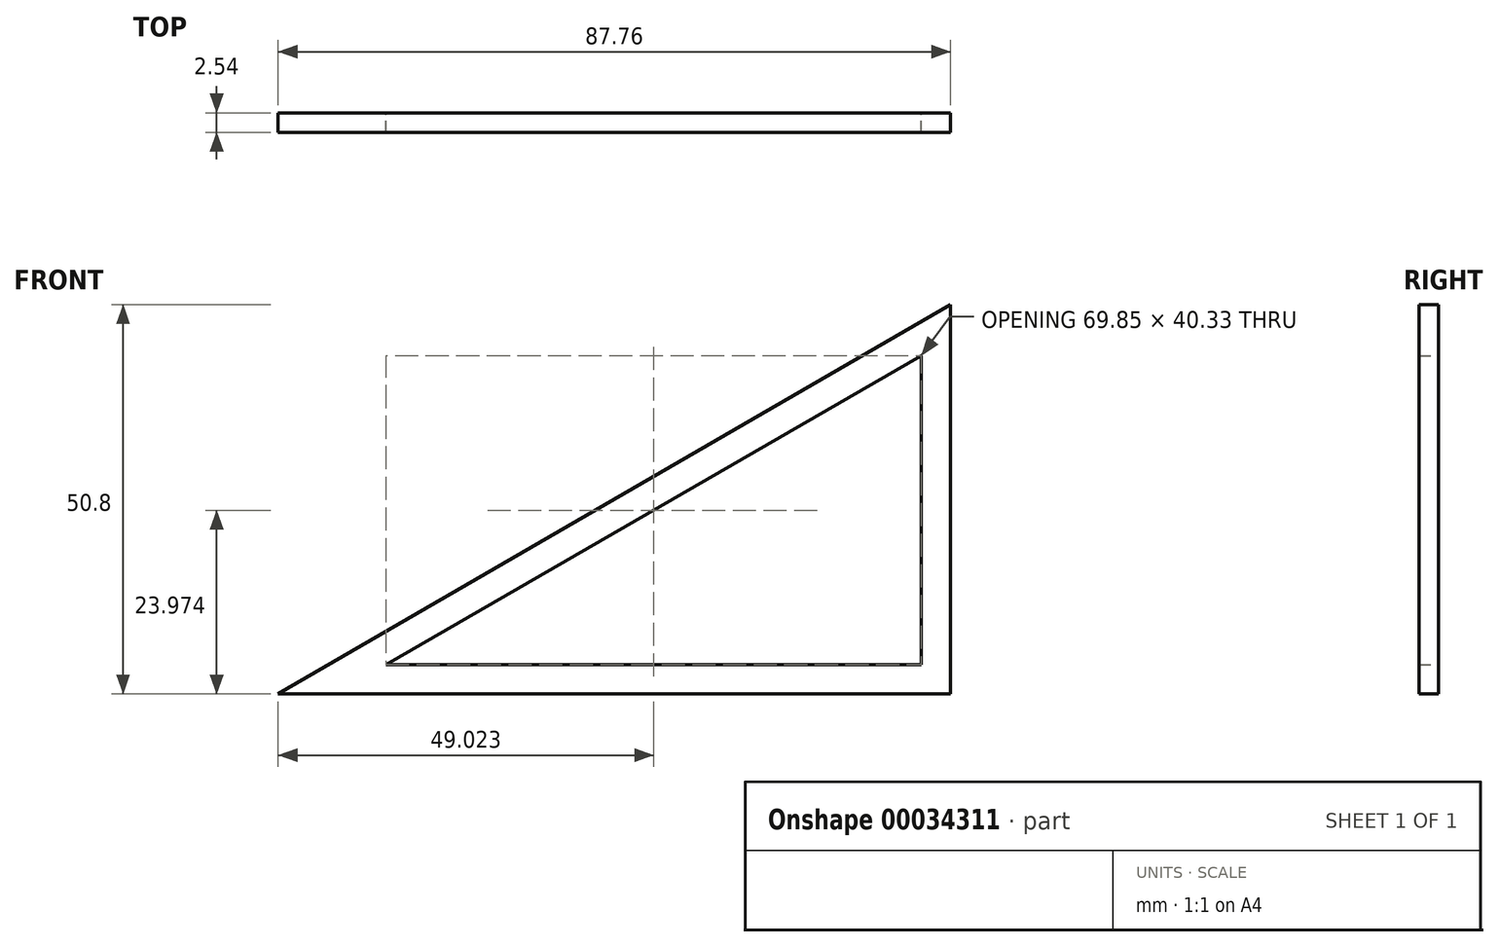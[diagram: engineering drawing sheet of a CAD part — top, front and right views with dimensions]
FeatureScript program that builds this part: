
annotation { "Feature Type Name" : "Feature", "Feature Type Description" : "" }
export const myFeature = defineFeature(function(context is Context, id is Id, definition is map)
    precondition{}
    {
        {
            var Q0;
            Q0=qCreatedBy(makeId("Front.planeOp"),FACE);
            var sketch = newSketch(context, id + "F0", { "sketchPlane" : qUnion([Q0])});
            skLineSegment(sketch, "E0", {"start": v(0, 0) * mm, "end": v(87.76, 0) * mm});
            skLineSegment(sketch, "E1", {"start": v(87.76, 0) * mm, "end": v(87.76, 50.8) * mm});
            skLineSegment(sketch, "E2", {"start": v(87.76, 50.8) * mm, "end": v(0, 0) * mm});
            skLineSegment(sketch, "E3", {"start": v(43.88, 0) * mm, "end": v(43.88, 0) * mm});
            skLineSegment(sketch, "E4", {"start": v(87.76, 25.4) * mm, "end": v(87.76, 0) * mm});
            skLineSegment(sketch, "E5", {"start": v(87.76, 0) * mm, "end": v(63.34, 0) * mm});
            skLineSegment(sketch, "E6", {"start": v(87.76, 50.8) * mm, "end": v(87.76, 0) * mm});
            skLineSegment(sketch, "E7", {"start": v(87.76, 25.4) * mm, "end": v(83.95, 25.4) * mm, "construction": true});
            skLineSegment(sketch, "E8", {"start": v(63.34, 0) * mm, "end": v(63.34, 3.8) * mm, "construction": true});
            skLineSegment(sketch, "E9", {"start": v(83.95, 25.4) * mm, "end": v(83.95, 44.14) * mm});
            skLineSegment(sketch, "E10", {"start": v(83.95, 44.14) * mm, "end": v(83.95, 3.81) * mm});
            skLineSegment(sketch, "E11", {"start": v(83.95, 3.81) * mm, "end": v(63.34, 3.8) * mm});
            skLineSegment(sketch, "E12", {"start": v(63.34, 3.8) * mm, "end": v(14.1, 3.8) * mm});
            skLineSegment(sketch, "E13", {"start": v(14.1, 3.8) * mm, "end": v(83.95, 44.14) * mm});
            skLineSegment(sketch, "E14", {"start": v(45.97, 26.6) * mm, "end": v(47.87, 23.31) * mm, "construction": true});
            skLineSegment(sketch, "E15", {"start": v(14.1, 3.8) * mm, "end": v(0, 0) * mm, "construction": true});
            skSolve(sketch);
        }
        {
            var Q0;
            Q0=makeQuery(id+"F0.imprint","IMPRINT",FACE,{"disambiguationData":[TD([[makeQuery(id+"F0.imprint","IMPRINT",EDGE,{"derivedFrom":sQuery(id+"F0.wireOp",EDGE,"E0")}),1.0]])]});
            extrude(context, id + "F1", {"entities" : qUnion([Q0]), "depth" : 2.54 * mm});
        }
    });
